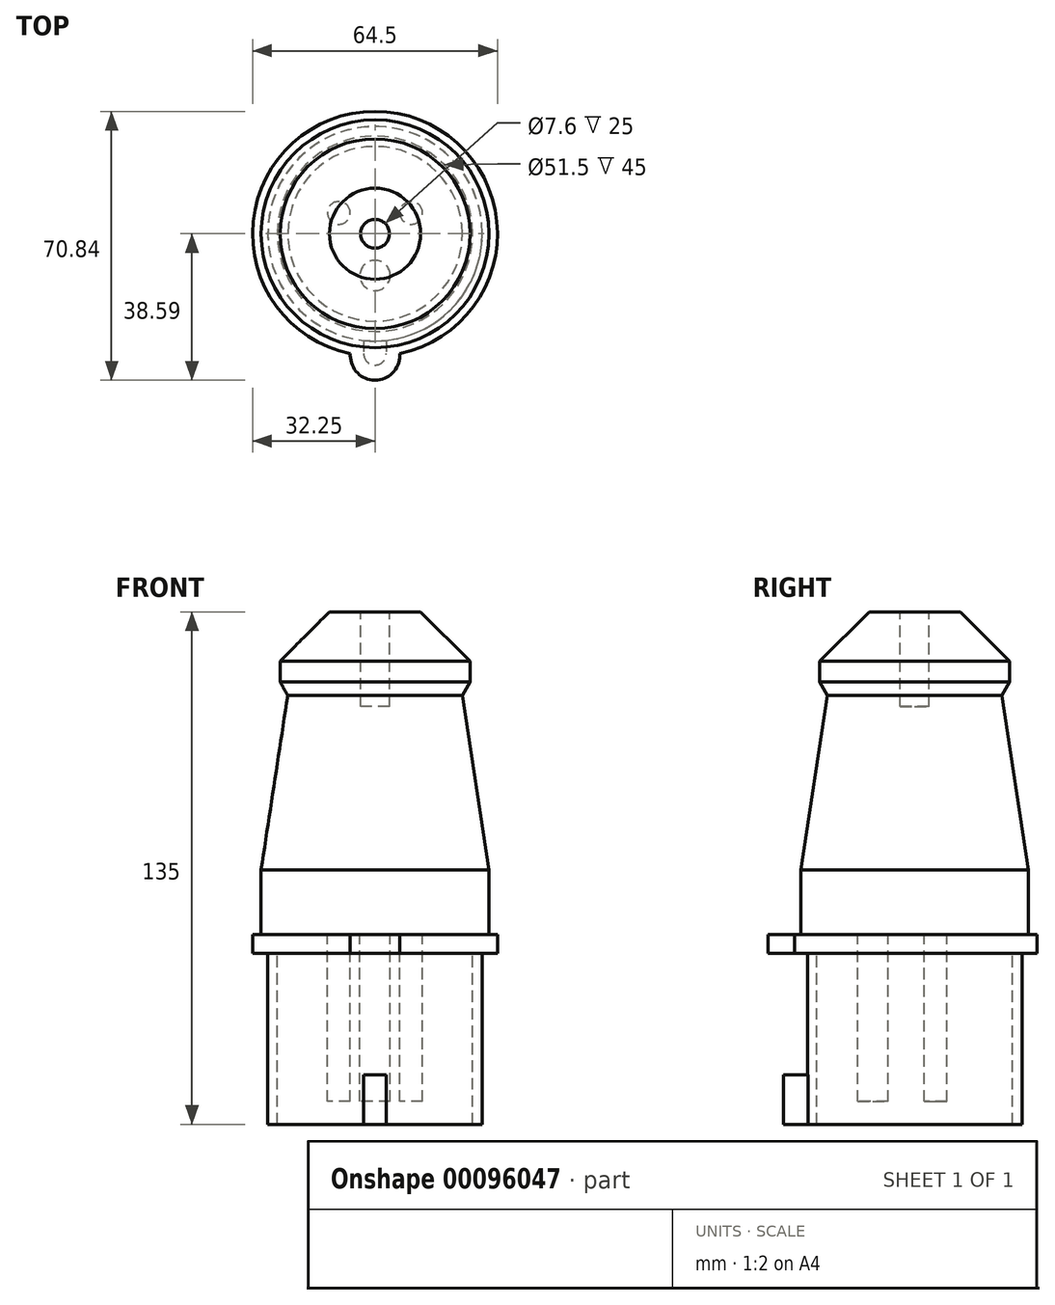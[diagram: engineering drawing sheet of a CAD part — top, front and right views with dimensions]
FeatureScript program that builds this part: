
annotation { "Feature Type Name" : "Feature", "Feature Type Description" : "" }
export const myFeature = defineFeature(function(context is Context, id is Id, definition is map)
    precondition{}
    {
        {
            var Q0;
            Q0=qCreatedBy(makeId("Top.planeOp"),FACE);
            var sketch = newSketch(context, id + "F0", { "sketchPlane" : qUnion([Q0])});
            skArc(sketch, "E0", {"start": v(6.5, -31.59) * mm, "mid": v(0, 32.25) * mm, "end": v(-6.5, -31.59) * mm});
            skLineSegment(sketch, "E1", {"start": v(-6.5, -31.59) * mm, "end": v(-6.5, -32.09) * mm});
            skLineSegment(sketch, "E2", {"start": v(6.5, -31.59) * mm, "end": v(6.5, -32.09) * mm});
            skArc(sketch, "E3", {"start": v(-6.5, -32.09) * mm, "mid": v(0, -38.59) * mm, "end": v(6.5, -32.09) * mm});
            skSolve(sketch);
        }
        {
            var Q0;
            Q0 = qSketchRegion(id + "F0", true);
            extrude(context, id + "F1", {"entities" : qUnion([Q0]), "oppositeDirection" : true, "depth" : 5 * mm});
        }
        {
            var Q0;
            Q0=makeQuery(id+"F1.opExtrude","CAP_FACE",FACE,{"disambiguationData":[OSD([sQuery(id+"F0.wireOp",EDGE,"E0"),sQuery(id+"F0.wireOp",EDGE,"E1"),sQuery(id+"F0.wireOp",EDGE,"E2"),sQuery(id+"F0.wireOp",EDGE,"E3")])],"isStart":true});
            var sketch = newSketch(context, id + "F2", { "sketchPlane" : qUnion([Q0])});
            skCircle(sketch, "E4", {"center": v(0, 0) * mm, "radius": 28.25 * mm});
            skCircle(sketch, "E5", {"center": v(0, 0) * mm, "radius": 25.75 * mm});
            skSolve(sketch);
        }
        {
            var Q0;
            Q0 = qSketchRegion(id + "F2", true);
            extrude(context, id + "F3", {"entities" : qUnion([Q0]), "operationType" : NewBodyOperationType.ADD, "oppositeDirection" : true, "depth" : 50 * mm});
        }
        {
            var Q0;
            Q0=makeQuery(id+"F3.opExtrude","CAP_FACE",FACE,{"disambiguationData":[OSD([sQuery(id+"F2.wireOp",EDGE,"E4"),sQuery(id+"F2.wireOp",EDGE,"E5")])],"isStart":false});
            var sketch = newSketch(context, id + "F4", { "sketchPlane" : qUnion([Q0])});
            skLineSegment(sketch, "E6", {"start": v(-3, 28.1) * mm, "end": v(-3, 31.6) * mm});
            skLineSegment(sketch, "E7", {"start": v(3, 28.1) * mm, "end": v(3, 31.6) * mm});
            skArc(sketch, "E8", {"start": v(-3, 31.6) * mm, "mid": v(0, 34.6) * mm, "end": v(3, 31.6) * mm});
            skArc(sketch, "E9", {"start": v(3, 28.1) * mm, "mid": v(0, 28.25) * mm, "end": v(-3, 28.1) * mm});
            skSolve(sketch);
        }
        {
            var Q0;
            Q0 = qSketchRegion(id + "F4", true);
            extrude(context, id + "F5", {"entities" : qUnion([Q0]), "operationType" : NewBodyOperationType.ADD, "oppositeDirection" : true, "depth" : 13 * mm});
        }
        {
            var Q0;
            Q0=makeQuery(id+"F3.boolean.opBoolean","SPLIT",FACE,{"disambiguationData":[TD([makeQuery(id+"F3.opExtrude","SWEPT_FACE",FACE,{"disambiguationData":[OSD([sQuery(id+"F2.wireOp",EDGE,"E5")])]})])],"derivedFrom":makeQuery(id+"F1.opExtrude","CAP_FACE",FACE,{"disambiguationData":[OSD([sQuery(id+"F0.wireOp",EDGE,"E0"),sQuery(id+"F0.wireOp",EDGE,"E1"),sQuery(id+"F0.wireOp",EDGE,"E2"),sQuery(id+"F0.wireOp",EDGE,"E3")])],"isStart":true})});
            var sketch = newSketch(context, id + "F6", { "sketchPlane" : qUnion([Q0])});
            skCircle(sketch, "E10", {"center": v(0, -11) * mm, "radius": 4 * mm});
            skCircle(sketch, "E11", {"center": v(9.53, 5.5) * mm, "radius": 3 * mm});
            skCircle(sketch, "E12", {"center": v(-9.53, 5.5) * mm, "radius": 3 * mm});
            skLineSegment(sketch, "E13", {"start": v(0, 0) * mm, "end": v(-9.53, 5.5) * mm, "construction": true});
            skLineSegment(sketch, "E14", {"start": v(0, 0) * mm, "end": v(9.53, 5.5) * mm, "construction": true});
            skSolve(sketch);
        }
        {
            var Q0;
            Q0 = qSketchRegion(id + "F6", true);
            extrude(context, id + "F7", {"entities" : qUnion([Q0]), "oppositeDirection" : true, "depth" : 44 * mm});
        }
        {
            var Q0;
            Q0=qCreatedBy(makeId("Right.planeOp"),FACE);
            var sketch = newSketch(context, id + "F8", { "sketchPlane" : qUnion([Q0])});
            skLineSegment(sketch, "E15", {"start": v(0, 0) * mm, "end": v(0, 85) * mm});
            skLineSegment(sketch, "E16", {"start": v(0, 85) * mm, "end": v(-12, 85) * mm});
            skLineSegment(sketch, "E17", {"start": v(0, 0) * mm, "end": v(-30, 0) * mm});
            skLineSegment(sketch, "E18", {"start": v(-30, 0) * mm, "end": v(-30, 17) * mm});
            skLineSegment(sketch, "E19", {"start": v(-12, 85) * mm, "end": v(-25, 72) * mm});
            skLineSegment(sketch, "E20", {"start": v(-25, 72) * mm, "end": v(-25, 66.5) * mm});
            skLineSegment(sketch, "E21", {"start": v(-25, 66.5) * mm, "end": v(-23, 63) * mm});
            skLineSegment(sketch, "E22", {"start": v(-23, 63) * mm, "end": v(-30, 17) * mm});
            skLineSegment(sketch, "E23", {"start": v(0, 0) * mm, "end": v(0, 144.1) * mm, "construction": true});
            skSolve(sketch);
        }
        {
            var Q0;
            Q0 = qSketchRegion(id + "F8", true);
            var Q1;
            Q1=sQuery(id+"F8.wireOp",EDGE,"E23");
            revolve(context, id + "F9", {"entities" : qUnion([Q0]), "axis" : qUnion([Q1]), "revolveType" : RevolveType.FULL});
        }
        {
            var Q0;
            Q0=makeQuery(id+"F9.opRevolve","SWEPT_FACE",FACE,{"disambiguationData":[OSD([sQuery(id+"F8.wireOp",EDGE,"E16")])]});
            var sketch = newSketch(context, id + "F10", { "sketchPlane" : qUnion([Q0])});
            skCircle(sketch, "E24", {"center": v(0, 0) * mm, "radius": 3.8 * mm});
            skSolve(sketch);
        }
        {
            var Q0;
            Q0 = qSketchRegion(id + "F10", true);
            extrude(context, id + "F11", {"entities" : qUnion([Q0]), "operationType" : NewBodyOperationType.REMOVE, "oppositeDirection" : true, "depth" : 25 * mm});
        }
    });
